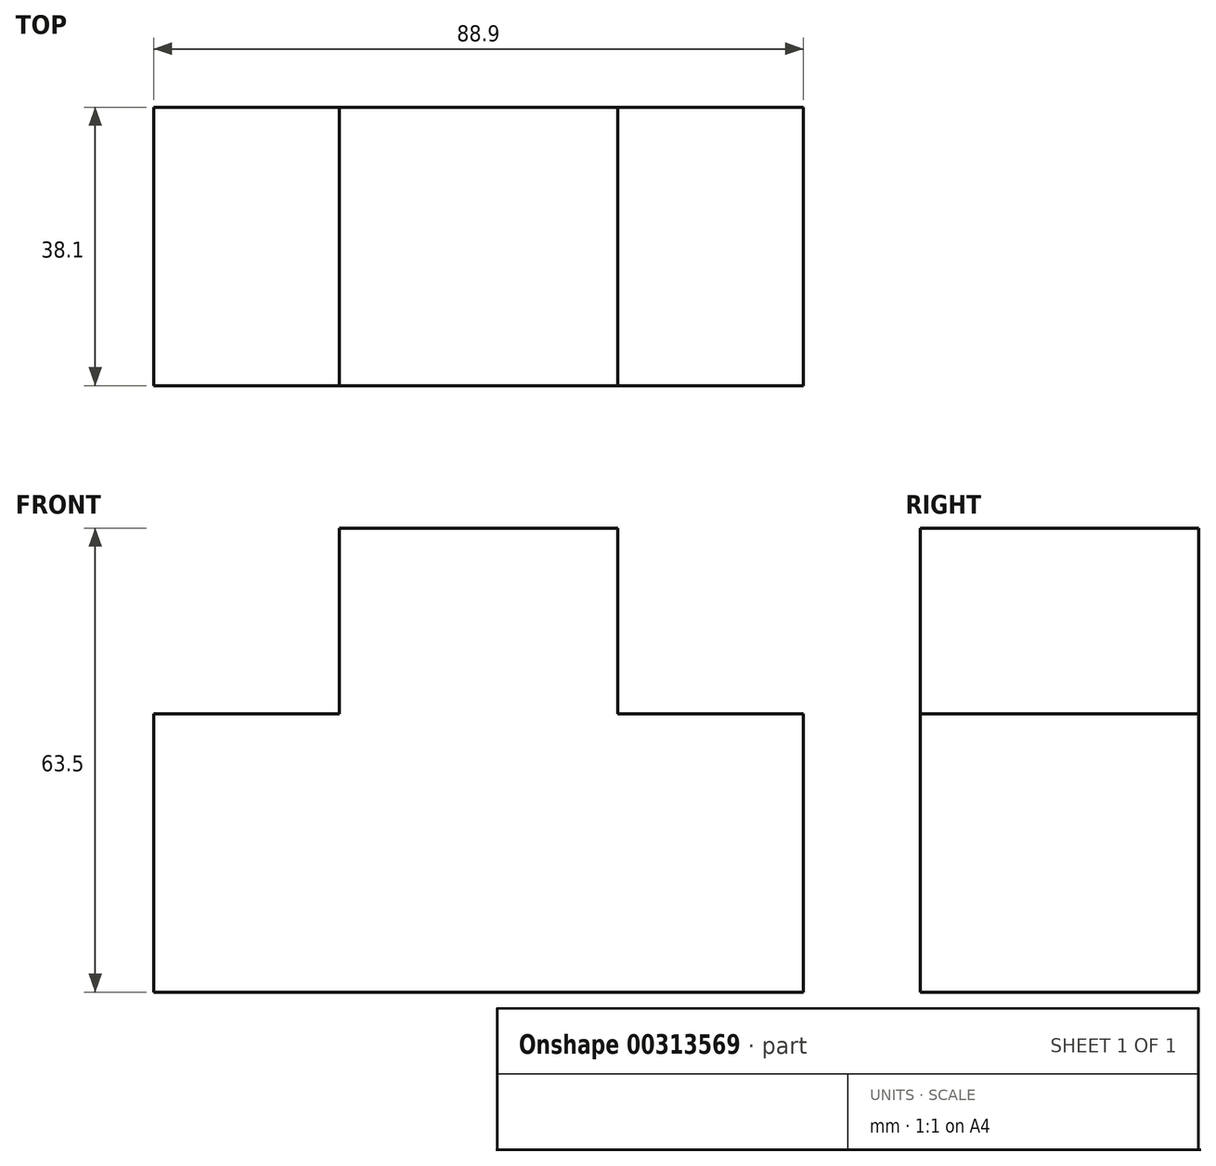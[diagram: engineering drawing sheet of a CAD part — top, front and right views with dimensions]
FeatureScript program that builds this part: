
annotation { "Feature Type Name" : "Feature", "Feature Type Description" : "" }
export const myFeature = defineFeature(function(context is Context, id is Id, definition is map)
    precondition{}
    {
        {
            var Q0;
            Q0=qCreatedBy(makeId("Front.planeOp"),FACE);
            var sketch = newSketch(context, id + "F0", { "sketchPlane" : qUnion([Q0])});
            skLineSegment(sketch, "E0", {"start": v(-19.05, 31.75) * mm, "end": v(19.05, 31.75) * mm});
            skLineSegment(sketch, "E1", {"start": v(19.05, 31.75) * mm, "end": v(19.05, 6.35) * mm});
            skLineSegment(sketch, "E2", {"start": v(19.05, 6.35) * mm, "end": v(44.45, 6.35) * mm});
            skLineSegment(sketch, "E3", {"start": v(44.45, 6.35) * mm, "end": v(44.45, -31.75) * mm});
            skLineSegment(sketch, "E4", {"start": v(44.45, -31.75) * mm, "end": v(-44.45, -31.75) * mm});
            skLineSegment(sketch, "E5", {"start": v(-44.45, -31.75) * mm, "end": v(-44.45, 6.35) * mm});
            skLineSegment(sketch, "E6", {"start": v(-44.45, 6.35) * mm, "end": v(-19.05, 6.35) * mm});
            skLineSegment(sketch, "E7", {"start": v(-19.05, 6.35) * mm, "end": v(-19.05, 31.75) * mm});
            skSolve(sketch);
        }
        {
            var Q0;
            Q0=makeQuery(id+"F0.imprint","IMPRINT",FACE,{"disambiguationData":[TD([[makeQuery(id+"F0.imprint","IMPRINT",EDGE,{"derivedFrom":sQuery(id+"F0.wireOp",EDGE,"E0")}),-1.0]])]});
            extrude(context, id + "F1", {"entities" : qUnion([Q0]), "depth" : 38.1 * mm});
        }
    });
